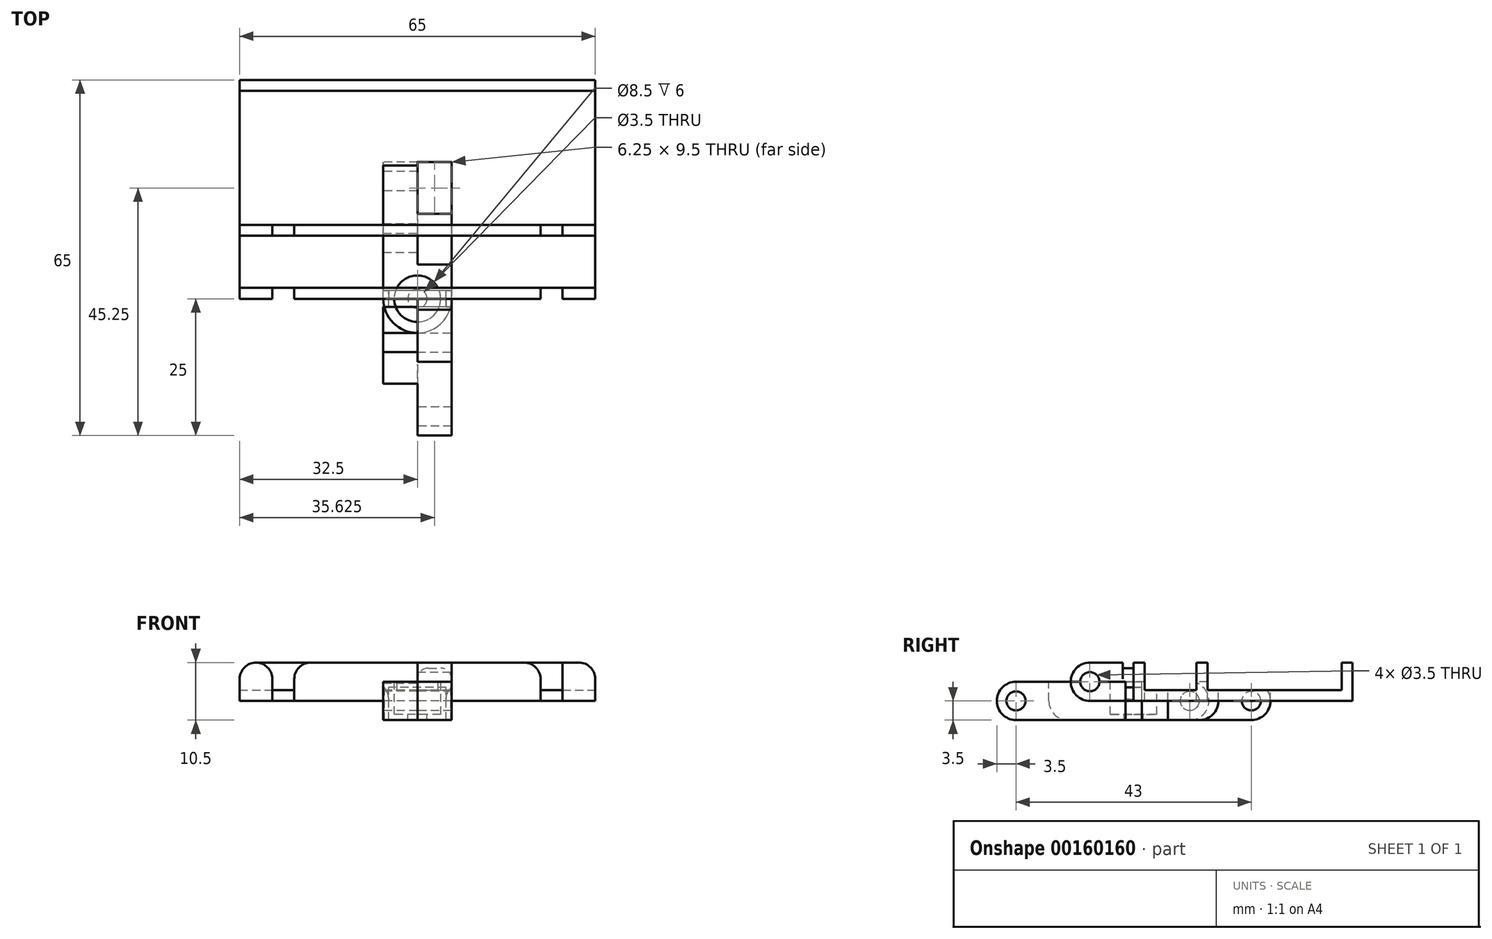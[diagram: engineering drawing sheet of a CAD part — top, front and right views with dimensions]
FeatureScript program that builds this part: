
annotation { "Feature Type Name" : "Feature", "Feature Type Description" : "" }
export const myFeature = defineFeature(function(context is Context, id is Id, definition is map)
    precondition{}
    {
        {
            var Q0;
            Q0=qCreatedBy(makeId("Top.planeOp"),FACE);
            var sketch = newSketch(context, id + "F0", { "sketchPlane" : qUnion([Q0])});
            skArc(sketch, "E0", {"start": v(-6.25, 0) * mm, "mid": v(0, -6.25) * mm, "end": v(6.25, 0) * mm});
            skLineSegment(sketch, "E1", {"start": v(-6.25, 0) * mm, "end": v(-6.25, 13.75) * mm});
            skLineSegment(sketch, "E2", {"start": v(-6.25, 13.75) * mm, "end": v(6.25, 13.75) * mm});
            skLineSegment(sketch, "E3", {"start": v(6.25, 13.75) * mm, "end": v(6.25, 0) * mm});
            skSolve(sketch);
        }
        {
            var Q0;
            Q0 = qSketchRegion(id + "F0", true);
            extrude(context, id + "F1", {"entities" : qUnion([Q0]), "endBound" : BoundingType.SYMMETRIC, "depth" : 7 * mm});
        }
        {
            var Q0;
            Q0=makeQuery(id+"F1.opExtrude","CAP_FACE",FACE,{"disambiguationData":[OSD([sQuery(id+"F0.wireOp",EDGE,"E0"),sQuery(id+"F0.wireOp",EDGE,"E1"),sQuery(id+"F0.wireOp",EDGE,"E2"),sQuery(id+"F0.wireOp",EDGE,"E3")])],"isStart":false});
            var sketch = newSketch(context, id + "F2", { "sketchPlane" : qUnion([Q0])});
            skCircle(sketch, "E4", {"center": v(0, 0) * mm, "radius": 4.25 * mm});
            skSolve(sketch);
        }
        {
            var Q0;
            Q0=makeQuery(id+"F2.imprint","IMPRINT",FACE,{"disambiguationData":[TD([[makeQuery(id+"F2.imprint","IMPRINT",EDGE,{"derivedFrom":sQuery(id+"F2.wireOp",EDGE,"E4")}),1.0]])]});
            extrude(context, id + "F3", {"entities" : qUnion([Q0]), "operationType" : NewBodyOperationType.REMOVE, "oppositeDirection" : true, "depth" : 6 * mm});
        }
        {
            var Q0;
            Q0=makeQuery(id+"F3.boolean.opBoolean","COPY",FACE,{"derivedFrom":makeQuery(id+"F3.opExtrude","CAP_FACE",FACE,{"disambiguationData":[OSD([sQuery(id+"F2.wireOp",EDGE,"E4")])],"isStart":false})});
            var sketch = newSketch(context, id + "F4", { "sketchPlane" : qUnion([Q0])});
            skCircle(sketch, "E5", {"center": v(0, 0) * mm, "radius": 1.75 * mm});
            skSolve(sketch);
        }
        {
            var Q0;
            Q0=makeQuery(id+"F4.imprint","IMPRINT",FACE,{"disambiguationData":[TD([[makeQuery(id+"F4.imprint","IMPRINT",EDGE,{"derivedFrom":sQuery(id+"F4.wireOp",EDGE,"E5")}),1.0]])]});
            extrude(context, id + "F5", {"entities" : qUnion([Q0]), "operationType" : NewBodyOperationType.REMOVE, "endBound" : BoundingType.THROUGH_ALL, "oppositeDirection" : true, "depth" : 25 * mm});
        }
        {
            var Q0;
            Q0=makeQuery(id+"F1.opExtrude","CAP_FACE",FACE,{"disambiguationData":[OSD([sQuery(id+"F0.wireOp",EDGE,"E0"),sQuery(id+"F0.wireOp",EDGE,"E1"),sQuery(id+"F0.wireOp",EDGE,"E2"),sQuery(id+"F0.wireOp",EDGE,"E3")])],"isStart":false});
            var sketch = newSketch(context, id + "F6", { "sketchPlane" : qUnion([Q0])});
            skLineSegment(sketch, "E6.bottom", {"start": v(6.25, 13.75) * mm, "end": v(0, 13.75) * mm});
            skLineSegment(sketch, "E6.top", {"start": v(6.25, 6.25) * mm, "end": v(0, 6.25) * mm});
            skLineSegment(sketch, "E6.left", {"start": v(6.25, 13.75) * mm, "end": v(6.25, 6.25) * mm});
            skLineSegment(sketch, "E6.right", {"start": v(0, 13.75) * mm, "end": v(0, 6.25) * mm});
            skSolve(sketch);
        }
        {
            var Q0;
            Q0=makeQuery(id+"F6.imprint","IMPRINT",FACE,{"disambiguationData":[TD([[makeQuery(id+"F6.imprint","IMPRINT",EDGE,{"derivedFrom":sQuery(id+"F6.wireOp",EDGE,"E6.bottom")}),-1.0]])]});
            extrude(context, id + "F7", {"entities" : qUnion([Q0]), "operationType" : NewBodyOperationType.REMOVE, "endBound" : BoundingType.THROUGH_ALL, "oppositeDirection" : true, "depth" : 25 * mm});
        }
        {
            var Q0;
            Q0=makeQuery(id+"F7.boolean.opBoolean","COPY",FACE,{"derivedFrom":makeQuery(id+"F7.opExtrude","SWEPT_FACE",FACE,{"disambiguationData":[OSD([sQuery(id+"F6.wireOp",EDGE,"E6.right")])]})});
            var sketch = newSketch(context, id + "F8", { "sketchPlane" : qUnion([Q0])});
            skCircle(sketch, "E7", {"center": v(10.25, 0) * mm, "radius": 1.75 * mm});
            skSolve(sketch);
        }
        {
            var Q0;
            Q0=makeQuery(id+"F8.imprint","IMPRINT",FACE,{"disambiguationData":[TD([[makeQuery(id+"F8.imprint","IMPRINT",EDGE,{"derivedFrom":sQuery(id+"F8.wireOp",EDGE,"E7")}),1.0]])]});
            extrude(context, id + "F9", {"entities" : qUnion([Q0]), "operationType" : NewBodyOperationType.REMOVE, "endBound" : BoundingType.THROUGH_ALL, "oppositeDirection" : true, "depth" : 25 * mm});
        }
        {
            var Q0;
            Q0=makeQuery(id+"F1.opExtrude","CAP_EDGE",EDGE,{"disambiguationData":[OSD([sQuery(id+"F0.wireOp",EDGE,"E2")])],"isStart":false});
            var Q1;
            Q1=makeQuery(id+"F1.opExtrude","CAP_EDGE",EDGE,{"disambiguationData":[OSD([sQuery(id+"F0.wireOp",EDGE,"E2")])],"isStart":true});
            fillet(context, id + "F10", {"entities" : qUnion([Q0, Q1]), "radius" : 3.5 * mm, "tangentPropagation" : true, "allowEdgeOverflow" : false});
        }
        {
            var Q0;
            Q0=qCreatedBy(makeId("Right.planeOp"),FACE);
            var sketch = newSketch(context, id + "F11", { "sketchPlane" : qUnion([Q0])});
            skLineSegment(sketch, "E8.bottom", {"start": v(21.5, 3.5) * mm, "end": v(1.5, 3.5) * mm});
            skLineSegment(sketch, "E8.top", {"start": v(21.5, -3.5) * mm, "end": v(-21.5, -3.5) * mm});
            skLineSegment(sketch, "E8.left", {"start": v(25, 0) * mm, "end": v(25, 0) * mm});
            skLineSegment(sketch, "E8.right", {"start": v(-25, 0) * mm, "end": v(-25, 0) * mm});
            skPoint(sketch, "E8.middle", {"position": v(0, 0) * mm});
            skPoint(sketch, "E9.visualSharp", {"position": v(-25, 3.5) * mm});
            skArc(sketch, "E9.filletArc", {"start": v(-21.5, 3.5) * mm, "mid": v(-23.97, 2.47) * mm, "end": v(-25, 0) * mm});
            skPoint(sketch, "E10.visualSharp", {"position": v(-25, -3.5) * mm});
            skArc(sketch, "E10.filletArc", {"start": v(-25, 0) * mm, "mid": v(-23.97, -2.47) * mm, "end": v(-21.5, -3.5) * mm});
            skPoint(sketch, "E11.visualSharp", {"position": v(25, -3.5) * mm});
            skArc(sketch, "E11.filletArc", {"start": v(21.5, -3.5) * mm, "mid": v(23.97, -2.47) * mm, "end": v(25, 0) * mm});
            skPoint(sketch, "E12.visualSharp", {"position": v(25, 3.5) * mm});
            skArc(sketch, "E12.filletArc", {"start": v(25, 0) * mm, "mid": v(23.97, 2.47) * mm, "end": v(21.5, 3.5) * mm});
            skCircle(sketch, "E13", {"center": v(-21.5, 0) * mm, "radius": 1.75 * mm});
            skCircle(sketch, "E14", {"center": v(21.5, 0) * mm, "radius": 1.75 * mm});
            skLineSegment(sketch, "E15", {"start": v(-1.5, 3.5) * mm, "end": v(-1.5, 2.5) * mm});
            skLineSegment(sketch, "E16", {"start": v(-1.5, 2.5) * mm, "end": v(1.5, 2.5) * mm});
            skLineSegment(sketch, "E17", {"start": v(1.5, 2.5) * mm, "end": v(1.5, 3.5) * mm});
            skLineSegment(sketch, "E18", {"start": v(0, 2.5) * mm, "end": v(0, 0) * mm, "construction": true});
            skLineSegment(sketch, "E19.trimOffspring", {"start": v(-1.5, 3.5) * mm, "end": v(-21.5, 3.5) * mm});
            skSolve(sketch);
        }
        {
            var Q0;
            Q0=makeQuery(id+"F11.imprint","IMPRINT",FACE,{"disambiguationData":[TD([[makeQuery(id+"F11.imprint","IMPRINT",EDGE,{"derivedFrom":sQuery(id+"F11.wireOp",EDGE,"E8.bottom")}),1.0]])]});
            extrude(context, id + "F12", {"entities" : qUnion([Q0]), "endBound" : BoundingType.SYMMETRIC, "depth" : 12.5 * mm});
        }
        {
            var Q0;
            Q0=makeQuery(id+"F12.opExtrude","SWEPT_FACE",FACE,{"disambiguationData":[OSD([sQuery(id+"F11.wireOp",EDGE,"E8.bottom")])]});
            var sketch = newSketch(context, id + "F13", { "sketchPlane" : qUnion([Q0])});
            skLineSegment(sketch, "E20", {"start": v(-6.25, 25) * mm, "end": v(6.25, 25) * mm, "construction": true});
            skLineSegment(sketch, "E21", {"start": v(6.25, -25) * mm, "end": v(-6.25, -25) * mm, "construction": true});
            skLineSegment(sketch, "E22.bottom", {"start": v(0, -15.5) * mm, "end": v(-6.25, -15.5) * mm});
            skLineSegment(sketch, "E22.top", {"start": v(0, -25) * mm, "end": v(-6.25, -25) * mm});
            skLineSegment(sketch, "E22.left", {"start": v(0, -15.5) * mm, "end": v(0, -25) * mm});
            skLineSegment(sketch, "E22.right", {"start": v(-6.25, -15.5) * mm, "end": v(-6.25, -25) * mm});
            skLineSegment(sketch, "E23.bottom", {"start": v(0, 15.5) * mm, "end": v(6.25, 15.5) * mm});
            skLineSegment(sketch, "E23.top", {"start": v(0, 25) * mm, "end": v(6.25, 25) * mm});
            skLineSegment(sketch, "E23.left", {"start": v(0, 15.5) * mm, "end": v(0, 25) * mm});
            skLineSegment(sketch, "E23.right", {"start": v(6.25, 15.5) * mm, "end": v(6.25, 25) * mm});
            skSolve(sketch);
        }
        {
            var Q0;
            Q0=qCreatedBy(makeId("Top.planeOp"),FACE);
            var sketch = newSketch(context, id + "F14", { "sketchPlane" : qUnion([Q0])});
            skLineSegment(sketch, "E24", {"start": v(-32.5, 40) * mm, "end": v(32.5, 40) * mm});
            skLineSegment(sketch, "E25", {"start": v(32.5, 40) * mm, "end": v(32.5, 0) * mm});
            skLineSegment(sketch, "E26", {"start": v(32.5, 0) * mm, "end": v(6.25, 0) * mm});
            skLineSegment(sketch, "E27", {"start": v(6.25, 0) * mm, "end": v(6.25, -11.5) * mm});
            skLineSegment(sketch, "E28", {"start": v(6.25, -11.5) * mm, "end": v(0, -11.5) * mm});
            skLineSegment(sketch, "E29", {"start": v(0, -11.5) * mm, "end": v(0, 0) * mm});
            skLineSegment(sketch, "E30", {"start": v(0, 0) * mm, "end": v(-32.5, 0) * mm});
            skLineSegment(sketch, "E31", {"start": v(-32.5, 0) * mm, "end": v(-32.5, 40) * mm});
            skSolve(sketch);
        }
        {
            var Q0;
            Q0=makeQuery(id+"F14.imprint","IMPRINT",FACE,{"disambiguationData":[TD([[makeQuery(id+"F14.imprint","IMPRINT",EDGE,{"derivedFrom":sQuery(id+"F14.wireOp",EDGE,"E24")}),-1.0]])]});
            extrude(context, id + "F15", {"entities" : qUnion([Q0]), "depth" : 7 * mm});
        }
        {
            var Q0;
            Q0=makeQuery(id+"F15.opExtrude","SWEPT_FACE",FACE,{"disambiguationData":[OSD([sQuery(id+"F14.wireOp",EDGE,"E25")])]});
            var sketch = newSketch(context, id + "F16", { "sketchPlane" : qUnion([Q0])});
            skCircle(sketch, "E32", {"center": v(-8, 3.5) * mm, "radius": 1.75 * mm});
            skPoint(sketch, "E32.centerSnap0", {"position": v(0, 3.5) * mm});
            skLineSegment(sketch, "E33.bottom", {"start": v(2, 7) * mm, "end": v(11.5, 7) * mm});
            skLineSegment(sketch, "E33.top", {"start": v(2, 2) * mm, "end": v(11.5, 2) * mm});
            skLineSegment(sketch, "E33.left", {"start": v(2, 7) * mm, "end": v(2, 2) * mm});
            skLineSegment(sketch, "E33.right", {"start": v(11.5, 7) * mm, "end": v(11.5, 2) * mm});
            skLineSegment(sketch, "E34.bottom", {"start": v(13.5, 7) * mm, "end": v(38, 7) * mm});
            skLineSegment(sketch, "E34.top", {"start": v(13.5, 2) * mm, "end": v(38, 2) * mm});
            skLineSegment(sketch, "E34.left", {"start": v(13.5, 7) * mm, "end": v(13.5, 2) * mm});
            skLineSegment(sketch, "E34.right", {"start": v(38, 7) * mm, "end": v(38, 2) * mm});
            skLineSegment(sketch, "E35.bottom", {"start": v(0, 7) * mm, "end": v(-2, 7) * mm});
            skLineSegment(sketch, "E35.top", {"start": v(0, 6) * mm, "end": v(-2, 6) * mm});
            skLineSegment(sketch, "E35.left", {"start": v(0, 7) * mm, "end": v(0, 6) * mm});
            skLineSegment(sketch, "E35.right", {"start": v(-2, 7) * mm, "end": v(-2, 6) * mm});
            skSolve(sketch);
        }
        {
            var Q0;
            Q0 = qSketchRegion(id + "F16", true);
            extrude(context, id + "F17", {"entities" : qUnion([Q0]), "operationType" : NewBodyOperationType.REMOVE, "endBound" : BoundingType.THROUGH_ALL, "oppositeDirection" : true, "depth" : 25 * mm});
        }
        {
            var Q0;
            Q0=makeQuery(id+"F17.boolean.opBoolean","INTERSECT",EDGE,{"derivedFrom":[makeQuery(id+"F15.opExtrude","SWEPT_FACE",FACE,{"disambiguationData":[OSD([sQuery(id+"F14.wireOp",EDGE,"E27")])]}),makeQuery(id+"F17.opExtrude","SWEPT_FACE",FACE,{"disambiguationData":[OSD([sQuery(id+"F16.wireOp",EDGE,"E35.top")])]})]});
            var Q1;
            Q1=makeQuery(id+"F17.boolean.opBoolean","INTERSECT",EDGE,{"derivedFrom":[makeQuery(id+"F15.opExtrude","SWEPT_FACE",FACE,{"disambiguationData":[OSD([sQuery(id+"F14.wireOp",EDGE,"E29")])]}),makeQuery(id+"F17.opExtrude","SWEPT_FACE",FACE,{"disambiguationData":[OSD([sQuery(id+"F16.wireOp",EDGE,"E35.top")])]})]});
            fillet(context, id + "F18", {"entities" : qUnion([Q0, Q1]), "radius" : 2 * mm, "tangentPropagation" : true, "allowEdgeOverflow" : false});
        }
        {
            var Q0;
            Q0=makeQuery(id+"F15.opExtrude","CAP_EDGE",EDGE,{"disambiguationData":[OSD([sQuery(id+"F14.wireOp",EDGE,"E28")])],"isStart":false});
            var Q1;
            Q1=makeQuery(id+"F15.opExtrude","CAP_EDGE",EDGE,{"disambiguationData":[OSD([sQuery(id+"F14.wireOp",EDGE,"E28")])],"isStart":true});
            fillet(context, id + "F19", {"entities" : qUnion([Q0, Q1]), "radius" : 3.5 * mm, "tangentPropagation" : true, "allowEdgeOverflow" : false});
        }
        {
            var Q0;
            {var subQ0=sQuery(id+"F14.wireOp",EDGE,"E26");var subQ1=sQuery(id+"F14.wireOp",EDGE,"E31");var subQ2=sQuery(id+"F14.wireOp",EDGE,"E30");var subQ3=sQuery(id+"F14.wireOp",EDGE,"E25");Q0=makeQuery(id+"F17.boolean.opBoolean","SPLIT",FACE,{"disambiguationData":[TD([makeQuery(id+"F15.opExtrude","SWEPT_FACE",FACE,{"disambiguationData":[OSD([subQ0])]})])],"derivedFrom":makeQuery(id+"F15.opExtrude","CAP_FACE",FACE,{"disambiguationData":[OSD([sQuery(id+"F14.wireOp",EDGE,"E24"),subQ3,subQ0,sQuery(id+"F14.wireOp",EDGE,"E27"),sQuery(id+"F14.wireOp",EDGE,"E28"),sQuery(id+"F14.wireOp",EDGE,"E29"),subQ2,subQ1])],"isStart":false})});}
            var sketch = newSketch(context, id + "F20", { "sketchPlane" : qUnion([Q0])});
            skLineSegment(sketch, "E36.bottom", {"start": v(-26.5, 0) * mm, "end": v(-22.5, 0) * mm});
            skLineSegment(sketch, "E36.top", {"start": v(-26.5, 2) * mm, "end": v(-22.5, 2) * mm});
            skLineSegment(sketch, "E36.left", {"start": v(-26.5, 0) * mm, "end": v(-26.5, 2) * mm});
            skLineSegment(sketch, "E36.right", {"start": v(-22.5, 0) * mm, "end": v(-22.5, 2) * mm});
            skLineSegment(sketch, "E37.bottom", {"start": v(22.5, 0) * mm, "end": v(26.5, 0) * mm});
            skLineSegment(sketch, "E37.top", {"start": v(22.5, 2) * mm, "end": v(26.5, 2) * mm});
            skLineSegment(sketch, "E37.left", {"start": v(22.5, 0) * mm, "end": v(22.5, 2) * mm});
            skLineSegment(sketch, "E37.right", {"start": v(26.5, 0) * mm, "end": v(26.5, 2) * mm});
            skLineSegment(sketch, "E38.0", {"start": v(-32.5, 13.5) * mm, "end": v(32.5, 13.5) * mm, "construction": true});
            skLineSegment(sketch, "E39.0", {"start": v(-32.5, 11.5) * mm, "end": v(32.5, 11.5) * mm, "construction": true});
            skLineSegment(sketch, "E40.bottom", {"start": v(-26.5, 11.5) * mm, "end": v(-22.5, 11.5) * mm});
            skLineSegment(sketch, "E40.top", {"start": v(-26.5, 13.5) * mm, "end": v(-22.5, 13.5) * mm});
            skLineSegment(sketch, "E40.left", {"start": v(-26.5, 11.5) * mm, "end": v(-26.5, 13.5) * mm});
            skLineSegment(sketch, "E40.right", {"start": v(-22.5, 11.5) * mm, "end": v(-22.5, 13.5) * mm});
            skLineSegment(sketch, "E41.bottom", {"start": v(22.5, 11.5) * mm, "end": v(26.5, 11.5) * mm, "construction": true});
            skLineSegment(sketch, "E41.top", {"start": v(22.5, 13.5) * mm, "end": v(26.5, 13.5) * mm, "construction": true});
            skLineSegment(sketch, "E41.left", {"start": v(22.5, 11.5) * mm, "end": v(22.5, 13.5) * mm});
            skLineSegment(sketch, "E41.right", {"start": v(26.5, 11.5) * mm, "end": v(26.5, 13.5) * mm});
            skLineSegment(sketch, "E42", {"start": v(-26.5, 2) * mm, "end": v(-26.5, 11.5) * mm, "construction": true});
            skLineSegment(sketch, "E43", {"start": v(-22.5, 11.5) * mm, "end": v(-22.5, 2) * mm, "construction": true});
            skLineSegment(sketch, "E44", {"start": v(22.5, 2) * mm, "end": v(22.5, 11.5) * mm, "construction": true});
            skLineSegment(sketch, "E45", {"start": v(26.5, 2) * mm, "end": v(26.5, 11.5) * mm, "construction": true});
            skLineSegment(sketch, "E46", {"start": v(22.5, 11.5) * mm, "end": v(26.5, 11.5) * mm});
            skLineSegment(sketch, "E47", {"start": v(26.5, 13.5) * mm, "end": v(22.5, 13.5) * mm});
            skSolve(sketch);
        }
        {
            var Q0;
            Q0 = qSketchRegion(id + "F20", true);
            extrude(context, id + "F21", {"entities" : qUnion([Q0]), "operationType" : NewBodyOperationType.REMOVE, "oppositeDirection" : true, "depth" : 25 * mm});
        }
        {
            var Q0;
            {var subQ0=sQuery(id+"F14.wireOp",EDGE,"E24");var subQ1=sQuery(id+"F14.wireOp",EDGE,"E31");Q0=makeQuery(id+"F17.boolean.opBoolean","SPLIT",EDGE,{"disambiguationData":[TD([makeQuery(id+"F15.opExtrude","SWEPT_FACE",FACE,{"disambiguationData":[OSD([subQ0])]})])],"derivedFrom":makeQuery(id+"F15.opExtrude","CAP_EDGE",EDGE,{"disambiguationData":[OSD([subQ1])],"isStart":false})});}
            var Q1;
            {var subQ0=sQuery(id+"F14.wireOp",EDGE,"E31");Q1=makeQuery(id+"F17.boolean.opBoolean","SPLIT",EDGE,{"disambiguationData":[TD([makeQuery(id+"F17.opExtrude","SWEPT_FACE",FACE,{"disambiguationData":[OSD([sQuery(id+"F16.wireOp",EDGE,"E33.right")])]})])],"derivedFrom":makeQuery(id+"F15.opExtrude","CAP_EDGE",EDGE,{"disambiguationData":[OSD([subQ0])],"isStart":false})});}
            var Q2;
            Q2=makeQuery(id+"F21.boolean.opBoolean","COPY",EDGE,{"derivedFrom":makeQuery(id+"F21.opExtrude","CAP_EDGE",EDGE,{"disambiguationData":[OSD([sQuery(id+"F20.wireOp",EDGE,"E40.left")])],"isStart":true})});
            var Q3;
            Q3=makeQuery(id+"F21.boolean.opBoolean","COPY",EDGE,{"derivedFrom":makeQuery(id+"F21.opExtrude","CAP_EDGE",EDGE,{"disambiguationData":[OSD([sQuery(id+"F20.wireOp",EDGE,"E40.right")])],"isStart":true})});
            var Q4;
            Q4=makeQuery(id+"F21.boolean.opBoolean","COPY",EDGE,{"derivedFrom":makeQuery(id+"F21.opExtrude","CAP_EDGE",EDGE,{"disambiguationData":[OSD([sQuery(id+"F20.wireOp",EDGE,"E41.left")])],"isStart":true})});
            var Q5;
            Q5=makeQuery(id+"F21.boolean.opBoolean","COPY",EDGE,{"derivedFrom":makeQuery(id+"F21.opExtrude","CAP_EDGE",EDGE,{"disambiguationData":[OSD([sQuery(id+"F20.wireOp",EDGE,"E41.right")])],"isStart":true})});
            var Q6;
            {var subQ0=sQuery(id+"F14.wireOp",EDGE,"E25");Q6=makeQuery(id+"F17.boolean.opBoolean","SPLIT",EDGE,{"disambiguationData":[TD([makeQuery(id+"F17.opExtrude","SWEPT_FACE",FACE,{"disambiguationData":[OSD([sQuery(id+"F16.wireOp",EDGE,"E33.right")])]})])],"derivedFrom":makeQuery(id+"F15.opExtrude","CAP_EDGE",EDGE,{"disambiguationData":[OSD([subQ0])],"isStart":false})});}
            var Q7;
            {var subQ0=sQuery(id+"F14.wireOp",EDGE,"E26");var subQ2=sQuery(id+"F14.wireOp",EDGE,"E25");Q7=makeQuery(id+"F17.boolean.opBoolean","SPLIT",EDGE,{"disambiguationData":[TD([makeQuery(id+"F15.opExtrude","SWEPT_FACE",FACE,{"disambiguationData":[OSD([subQ0])]})])],"derivedFrom":makeQuery(id+"F15.opExtrude","CAP_EDGE",EDGE,{"disambiguationData":[OSD([subQ2])],"isStart":false})});}
            var Q8;
            Q8=makeQuery(id+"F21.boolean.opBoolean","COPY",EDGE,{"derivedFrom":makeQuery(id+"F21.opExtrude","CAP_EDGE",EDGE,{"disambiguationData":[OSD([sQuery(id+"F20.wireOp",EDGE,"E37.right")])],"isStart":true})});
            var Q9;
            Q9=makeQuery(id+"F21.boolean.opBoolean","COPY",EDGE,{"derivedFrom":makeQuery(id+"F21.opExtrude","CAP_EDGE",EDGE,{"disambiguationData":[OSD([sQuery(id+"F20.wireOp",EDGE,"E37.left")])],"isStart":true})});
            var Q10;
            Q10=makeQuery(id+"F21.boolean.opBoolean","COPY",EDGE,{"derivedFrom":makeQuery(id+"F21.opExtrude","CAP_EDGE",EDGE,{"disambiguationData":[OSD([sQuery(id+"F20.wireOp",EDGE,"E36.right")])],"isStart":true})});
            var Q11;
            {var subQ0=sQuery(id+"F14.wireOp",EDGE,"E24");var subQ1=sQuery(id+"F14.wireOp",EDGE,"E25");Q11=makeQuery(id+"F17.boolean.opBoolean","SPLIT",EDGE,{"disambiguationData":[TD([makeQuery(id+"F15.opExtrude","SWEPT_FACE",FACE,{"disambiguationData":[OSD([subQ0])]})])],"derivedFrom":makeQuery(id+"F15.opExtrude","CAP_EDGE",EDGE,{"disambiguationData":[OSD([subQ1])],"isStart":false})});}
            var Q12;
            Q12=makeQuery(id+"F21.boolean.opBoolean","COPY",EDGE,{"derivedFrom":makeQuery(id+"F21.opExtrude","CAP_EDGE",EDGE,{"disambiguationData":[OSD([sQuery(id+"F20.wireOp",EDGE,"E36.left")])],"isStart":true})});
            var Q13;
            {var subQ0=sQuery(id+"F14.wireOp",EDGE,"E26");var subQ1=sQuery(id+"F14.wireOp",EDGE,"E31");Q13=makeQuery(id+"F17.boolean.opBoolean","SPLIT",EDGE,{"disambiguationData":[TD([makeQuery(id+"F15.opExtrude","SWEPT_FACE",FACE,{"disambiguationData":[OSD([subQ0])]})])],"derivedFrom":makeQuery(id+"F15.opExtrude","CAP_EDGE",EDGE,{"disambiguationData":[OSD([subQ1])],"isStart":false})});}
            fillet(context, id + "F22", {"entities" : qUnion([Q0, Q1, Q2, Q3, Q4, Q5, Q6, Q7, Q8, Q9, Q10, Q11, Q12, Q13]), "radius" : 3 * mm, "tangentPropagation" : true, "allowEdgeOverflow" : false});
        }
        {
            var Q0;
            Q0=makeQuery(id+"F12.opExtrude","SWEPT_FACE",FACE,{"disambiguationData":[OSD([sQuery(id+"F11.wireOp",EDGE,"E16")])]});
            var sketch = newSketch(context, id + "F23", { "sketchPlane" : qUnion([Q0])});
            skLineSegment(sketch, "E48.bottom", {"start": v(-6.25, 1.5) * mm, "end": v(-5.25, 1.5) * mm});
            skLineSegment(sketch, "E48.top", {"start": v(-6.25, -1.5) * mm, "end": v(-5.25, -1.5) * mm});
            skLineSegment(sketch, "E48.left", {"start": v(-6.25, 1.5) * mm, "end": v(-6.25, -1.5) * mm});
            skLineSegment(sketch, "E48.right", {"start": v(-5.25, 1.5) * mm, "end": v(-5.25, -1.5) * mm});
            skLineSegment(sketch, "E49.bottom", {"start": v(6.25, 1.5) * mm, "end": v(5.25, 1.5) * mm});
            skLineSegment(sketch, "E49.top", {"start": v(6.25, -1.5) * mm, "end": v(5.25, -1.5) * mm});
            skLineSegment(sketch, "E49.left", {"start": v(6.25, 1.5) * mm, "end": v(6.25, -1.5) * mm});
            skLineSegment(sketch, "E49.right", {"start": v(5.25, 1.5) * mm, "end": v(5.25, -1.5) * mm});
            skSolve(sketch);
        }
        {
            var Q0;
            Q0 = qSketchRegion(id + "F23", true);
            extrude(context, id + "F24", {"entities" : qUnion([Q0]), "operationType" : NewBodyOperationType.REMOVE, "endBound" : BoundingType.THROUGH_ALL, "oppositeDirection" : true, "depth" : 25 * mm});
        }
        {
            var Q0;
            Q0=makeQuery(id+"F24.boolean.opBoolean","COPY",EDGE,{"derivedFrom":makeQuery(id+"F24.opExtrude","CAP_EDGE",EDGE,{"disambiguationData":[OSD([sQuery(id+"F23.wireOp",EDGE,"E49.right")])],"isStart":true})});
            var Q1;
            Q1=makeQuery(id+"F24.boolean.opBoolean","COPY",EDGE,{"derivedFrom":makeQuery(id+"F24.opExtrude","CAP_EDGE",EDGE,{"disambiguationData":[OSD([sQuery(id+"F23.wireOp",EDGE,"E48.right")])],"isStart":true})});
            fillet(context, id + "F25", {"entities" : qUnion([Q0, Q1]), "radius" : 3 * mm, "tangentPropagation" : true, "allowEdgeOverflow" : false});
        }
        {
            var Q0;
            Q0 = qSketchRegion(id + "F13", true);
            extrude(context, id + "F26", {"entities" : qUnion([Q0]), "operationType" : NewBodyOperationType.REMOVE, "endBound" : BoundingType.THROUGH_ALL, "oppositeDirection" : true, "depth" : 25 * mm});
        }
        {
            var Q0;
            Q0=makeQuery(id+"F26.boolean.opBoolean","COPY",EDGE,{"derivedFrom":makeQuery(id+"F26.opExtrude","CAP_EDGE",EDGE,{"disambiguationData":[OSD([sQuery(id+"F13.wireOp",EDGE,"E23.bottom")])],"isStart":true})});
            var Q1;
            Q1=makeQuery(id+"F26.boolean.opBoolean","COPY",EDGE,{"derivedFrom":makeQuery(id+"F26.opExtrude","CAP_EDGE",EDGE,{"disambiguationData":[OSD([sQuery(id+"F13.wireOp",EDGE,"E22.bottom")])],"isStart":true})});
            var Q2;
            Q2=makeQuery(id+"F26.boolean.opBoolean","INTERSECT",EDGE,{"derivedFrom":[makeQuery(id+"F12.opExtrude","SWEPT_FACE",FACE,{"disambiguationData":[OSD([sQuery(id+"F11.wireOp",EDGE,"E8.top")])]}),makeQuery(id+"F26.opExtrude","SWEPT_FACE",FACE,{"disambiguationData":[OSD([sQuery(id+"F13.wireOp",EDGE,"E22.bottom")])]})]});
            var Q3;
            Q3=makeQuery(id+"F26.boolean.opBoolean","INTERSECT",EDGE,{"derivedFrom":[makeQuery(id+"F12.opExtrude","SWEPT_FACE",FACE,{"disambiguationData":[OSD([sQuery(id+"F11.wireOp",EDGE,"E8.top")])]}),makeQuery(id+"F26.opExtrude","SWEPT_FACE",FACE,{"disambiguationData":[OSD([sQuery(id+"F13.wireOp",EDGE,"E23.bottom")])]})]});
            fillet(context, id + "F27", {"entities" : qUnion([Q0, Q1, Q2, Q3]), "radius" : 3.5 * mm, "tangentPropagation" : true, "allowEdgeOverflow" : false});
        }
    });
